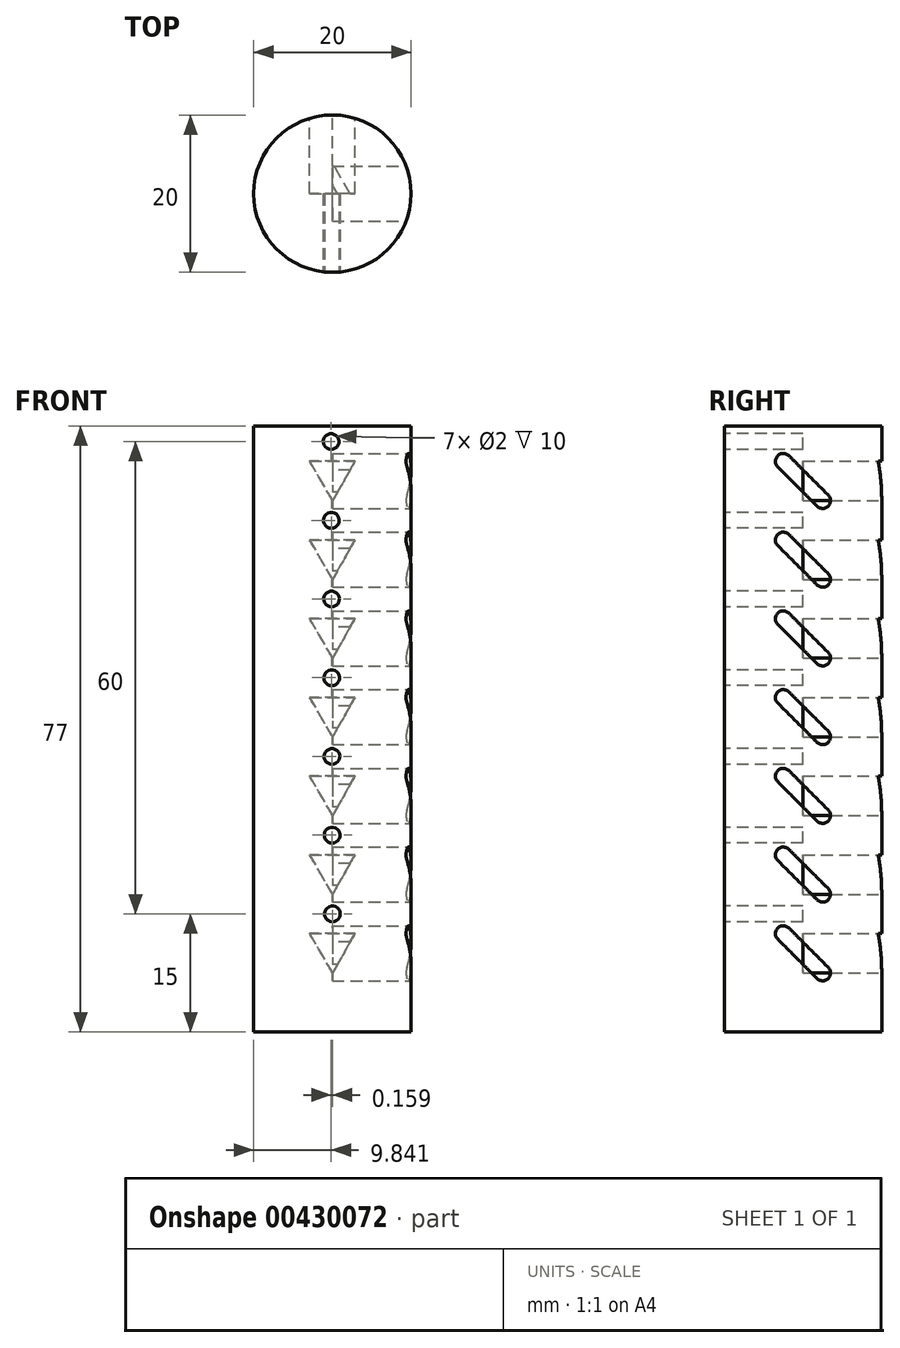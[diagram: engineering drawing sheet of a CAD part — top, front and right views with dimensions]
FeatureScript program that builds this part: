
annotation { "Feature Type Name" : "Feature", "Feature Type Description" : "" }
export const myFeature = defineFeature(function(context is Context, id is Id, definition is map)
    precondition{}
    {
        {
            var Q0;
            Q0=qCreatedBy(makeId("Top.planeOp"),FACE);
            var sketch = newSketch(context, id + "F0", { "sketchPlane" : qUnion([Q0])});
            skCircle(sketch, "E0", {"center": v(0, 0) * mm, "radius": 10 * mm});
            skSolve(sketch);
        }
        {
            var Q0;
            Q0=makeQuery(id+"F0.imprint","IMPRINT",FACE,{"disambiguationData":[TD([[makeQuery(id+"F0.imprint","IMPRINT",EDGE,{"derivedFrom":sQuery(id+"F0.wireOp",EDGE,"E0")}),1.0]])]});
            extrude(context, id + "F1", {"entities" : qUnion([Q0]), "depth" : (7 * 10 + 7) * mm});
        }
        {
            var Q0;
            Q0=qCreatedBy(makeId("Front.planeOp"),FACE);
            cPlane(context, id + "F2", {"entities" : qUnion([Q0]), "cplaneType" : CPlaneType.OFFSET, "offset" : 10 * mm, "width" : 150 * mm, "height" : 150 * mm});
        }
        {
            var Q0;
            Q0=qCreatedBy(id+"F2.planeOp",FACE);
            var sketch = newSketch(context, id + "F3", { "sketchPlane" : qUnion([Q0])});
            skCircle(sketch, "E1", {"center": v(0, 15) * mm, "radius": 1 * mm});
            skCircle(sketch, "E2.1.0.0", {"center": v(-0.03, 25) * mm, "radius": 1 * mm});
            skCircle(sketch, "E2.2.0.0", {"center": v(-0.05, 35) * mm, "radius": 1 * mm});
            skCircle(sketch, "E2.3.0.0", {"center": v(-0.08, 45) * mm, "radius": 1 * mm});
            skCircle(sketch, "E2.4.0.0", {"center": v(-0.1, 55) * mm, "radius": 1 * mm});
            skCircle(sketch, "E2.5.0.0", {"center": v(-0.13, 65) * mm, "radius": 1 * mm});
            skCircle(sketch, "E2.6.0.0", {"center": v(-0.16, 75) * mm, "radius": 1 * mm});
            skLineSegment(sketch, "E2.direction1", {"start": v(0, 15) * mm, "end": v(-0.03, 25) * mm, "construction": true});
            skSolve(sketch);
        }
        {
            var Q0;
            Q0=qSketchRegion(id+"F3",true);
            extrude(context, id + "F4", {"entities" : qUnion([Q0]), "operationType" : NewBodyOperationType.REMOVE, "oppositeDirection" : true, "depth" : 10 * mm});
        }
        {
            var Q0;
            Q0=qCreatedBy(makeId("Right.planeOp"),FACE);
            cPlane(context, id + "F5", {"entities" : qUnion([Q0]), "cplaneType" : CPlaneType.OFFSET, "offset" : 10 * mm, "width" : 150 * mm, "height" : 150 * mm});
        }
        {
            var Q0;
            Q0=qCreatedBy(id+"F5.planeOp",FACE);
            var sketch = newSketch(context, id + "F6", { "sketchPlane" : qUnion([Q0])});
            skLineSegment(sketch, "E3", {"start": v(-2.5, 12.5) * mm, "end": v(2.5, 7.5) * mm, "construction": true});
            skLineSegment(sketch, "E4", {"start": v(2.5, 7.5) * mm, "end": v(0, 7.5) * mm, "construction": true});
            skPoint(sketch, "E4.endSnap0", {"position": v(0, 10) * mm});
            skArc(sketch, "E5.0.startCap", {"start": v(-3.2, 11.8) * mm, "mid": v(-3.2, 13.2) * mm, "end": v(-1.8, 13.2) * mm});
            skArc(sketch, "E5.0.endCap", {"start": v(3.2, 8.2) * mm, "mid": v(3.2, 6.8) * mm, "end": v(1.8, 6.8) * mm});
            skLineSegment(sketch, "E5.0.left", {"start": v(-1.8, 13.2) * mm, "end": v(3.2, 8.2) * mm});
            skLineSegment(sketch, "E5.0.right", {"start": v(-3.2, 11.8) * mm, "end": v(1.8, 6.8) * mm});
            skLineSegment(sketch, "E6.1.0.0", {"start": v(-2.5, 22.5) * mm, "end": v(2.5, 17.5) * mm, "construction": true});
            skArc(sketch, "E6.1.0.1", {"start": v(-3.2, 21.8) * mm, "mid": v(-3.2, 23.2) * mm, "end": v(-1.8, 23.2) * mm});
            skLineSegment(sketch, "E6.1.0.2", {"start": v(-3.2, 21.8) * mm, "end": v(1.8, 16.8) * mm});
            skLineSegment(sketch, "E6.1.0.3", {"start": v(-1.8, 23.2) * mm, "end": v(3.2, 18.2) * mm});
            skLineSegment(sketch, "E6.1.0.4", {"start": v(2.5, 17.5) * mm, "end": v(0, 17.5) * mm, "construction": true});
            skPoint(sketch, "E6.1.0.5", {"position": v(0, 20) * mm});
            skArc(sketch, "E6.1.0.6", {"start": v(3.2, 18.2) * mm, "mid": v(3.2, 16.8) * mm, "end": v(1.8, 16.8) * mm});
            skLineSegment(sketch, "E6.2.0.0", {"start": v(-2.5, 32.5) * mm, "end": v(2.5, 27.5) * mm, "construction": true});
            skArc(sketch, "E6.2.0.1", {"start": v(-3.2, 31.8) * mm, "mid": v(-3.2, 33.2) * mm, "end": v(-1.8, 33.2) * mm});
            skLineSegment(sketch, "E6.2.0.2", {"start": v(-3.2, 31.8) * mm, "end": v(1.8, 26.8) * mm});
            skLineSegment(sketch, "E6.2.0.3", {"start": v(-1.8, 33.2) * mm, "end": v(3.2, 28.2) * mm});
            skLineSegment(sketch, "E6.2.0.4", {"start": v(2.5, 27.5) * mm, "end": v(0, 27.5) * mm, "construction": true});
            skPoint(sketch, "E6.2.0.5", {"position": v(0, 30) * mm});
            skArc(sketch, "E6.2.0.6", {"start": v(3.2, 28.2) * mm, "mid": v(3.2, 26.8) * mm, "end": v(1.8, 26.8) * mm});
            skLineSegment(sketch, "E6.3.0.0", {"start": v(-2.5, 42.5) * mm, "end": v(2.5, 37.5) * mm, "construction": true});
            skArc(sketch, "E6.3.0.1", {"start": v(-3.2, 41.8) * mm, "mid": v(-3.2, 43.2) * mm, "end": v(-1.8, 43.2) * mm});
            skLineSegment(sketch, "E6.3.0.2", {"start": v(-3.2, 41.8) * mm, "end": v(1.8, 36.8) * mm});
            skLineSegment(sketch, "E6.3.0.3", {"start": v(-1.8, 43.2) * mm, "end": v(3.2, 38.2) * mm});
            skLineSegment(sketch, "E6.3.0.4", {"start": v(2.5, 37.5) * mm, "end": v(0, 37.5) * mm, "construction": true});
            skPoint(sketch, "E6.3.0.5", {"position": v(0, 40) * mm});
            skArc(sketch, "E6.3.0.6", {"start": v(3.2, 38.2) * mm, "mid": v(3.2, 36.8) * mm, "end": v(1.8, 36.8) * mm});
            skLineSegment(sketch, "E6.4.0.0", {"start": v(-2.5, 52.5) * mm, "end": v(2.5, 47.5) * mm, "construction": true});
            skArc(sketch, "E6.4.0.1", {"start": v(-3.2, 51.8) * mm, "mid": v(-3.2, 53.2) * mm, "end": v(-1.8, 53.2) * mm});
            skLineSegment(sketch, "E6.4.0.2", {"start": v(-3.2, 51.8) * mm, "end": v(1.8, 46.8) * mm});
            skLineSegment(sketch, "E6.4.0.3", {"start": v(-1.8, 53.2) * mm, "end": v(3.2, 48.2) * mm});
            skLineSegment(sketch, "E6.4.0.4", {"start": v(2.5, 47.5) * mm, "end": v(0, 47.5) * mm, "construction": true});
            skPoint(sketch, "E6.4.0.5", {"position": v(0, 50) * mm});
            skArc(sketch, "E6.4.0.6", {"start": v(3.2, 48.2) * mm, "mid": v(3.2, 46.8) * mm, "end": v(1.8, 46.8) * mm});
            skLineSegment(sketch, "E6.5.0.0", {"start": v(-2.5, 62.5) * mm, "end": v(2.5, 57.5) * mm, "construction": true});
            skArc(sketch, "E6.5.0.1", {"start": v(-3.2, 61.8) * mm, "mid": v(-3.2, 63.2) * mm, "end": v(-1.8, 63.2) * mm});
            skLineSegment(sketch, "E6.5.0.2", {"start": v(-3.2, 61.8) * mm, "end": v(1.8, 56.8) * mm});
            skLineSegment(sketch, "E6.5.0.3", {"start": v(-1.8, 63.2) * mm, "end": v(3.2, 58.2) * mm});
            skLineSegment(sketch, "E6.5.0.4", {"start": v(2.5, 57.5) * mm, "end": v(0, 57.5) * mm, "construction": true});
            skPoint(sketch, "E6.5.0.5", {"position": v(0, 60) * mm});
            skArc(sketch, "E6.5.0.6", {"start": v(3.2, 58.2) * mm, "mid": v(3.2, 56.8) * mm, "end": v(1.8, 56.8) * mm});
            skLineSegment(sketch, "E6.6.0.0", {"start": v(-2.5, 72.5) * mm, "end": v(2.5, 67.5) * mm, "construction": true});
            skArc(sketch, "E6.6.0.1", {"start": v(-3.2, 71.8) * mm, "mid": v(-3.2, 73.2) * mm, "end": v(-1.8, 73.2) * mm});
            skLineSegment(sketch, "E6.6.0.2", {"start": v(-3.2, 71.8) * mm, "end": v(1.8, 66.8) * mm});
            skLineSegment(sketch, "E6.6.0.3", {"start": v(-1.8, 73.2) * mm, "end": v(3.2, 68.2) * mm});
            skLineSegment(sketch, "E6.6.0.4", {"start": v(2.5, 67.5) * mm, "end": v(0, 67.5) * mm, "construction": true});
            skPoint(sketch, "E6.6.0.5", {"position": v(0, 70) * mm});
            skArc(sketch, "E6.6.0.6", {"start": v(3.2, 68.2) * mm, "mid": v(3.2, 66.8) * mm, "end": v(1.8, 66.8) * mm});
            skLineSegment(sketch, "E6.direction1", {"start": v(0, 7.5) * mm, "end": v(0, 17.5) * mm, "construction": true});
            skSolve(sketch);
        }
        {
            var Q0;
            Q0=qSketchRegion(id+"F6",true);
            extrude(context, id + "F7", {"entities" : qUnion([Q0]), "operationType" : NewBodyOperationType.REMOVE, "oppositeDirection" : true, "depth" : 10 * mm});
        }
        {
            var Q0;
            Q0=qCreatedBy(makeId("Front.planeOp"),FACE);
            cPlane(context, id + "F8", {"entities" : qUnion([Q0]), "cplaneType" : CPlaneType.OFFSET, "offset" : 10 * mm, "oppositeDirection" : true, "width" : 150 * mm, "height" : 150 * mm});
        }
        {
            var Q0;
            Q0=qCreatedBy(id+"F8.planeOp",FACE);
            var sketch = newSketch(context, id + "F9", { "sketchPlane" : qUnion([Q0])});
            skLineSegment(sketch, "E7", {"start": v(-2.89, 12.5) * mm, "end": v(0, 7.5) * mm});
            skLineSegment(sketch, "E8", {"start": v(0, 7.5) * mm, "end": v(2.89, 12.5) * mm});
            skLineSegment(sketch, "E9", {"start": v(2.89, 12.5) * mm, "end": v(-2.89, 12.5) * mm});
            skLineSegment(sketch, "E10.1.0.0", {"start": v(0, 17.5) * mm, "end": v(2.89, 22.5) * mm});
            skLineSegment(sketch, "E10.1.0.1", {"start": v(2.89, 22.5) * mm, "end": v(-2.89, 22.5) * mm});
            skLineSegment(sketch, "E10.1.0.2", {"start": v(-2.89, 22.5) * mm, "end": v(0, 17.5) * mm});
            skLineSegment(sketch, "E10.2.0.0", {"start": v(0, 27.5) * mm, "end": v(2.89, 32.5) * mm});
            skLineSegment(sketch, "E10.2.0.1", {"start": v(2.89, 32.5) * mm, "end": v(-2.89, 32.5) * mm});
            skLineSegment(sketch, "E10.2.0.2", {"start": v(-2.89, 32.5) * mm, "end": v(0, 27.5) * mm});
            skLineSegment(sketch, "E10.3.0.0", {"start": v(0, 37.5) * mm, "end": v(2.89, 42.5) * mm});
            skLineSegment(sketch, "E10.3.0.1", {"start": v(2.89, 42.5) * mm, "end": v(-2.89, 42.5) * mm});
            skLineSegment(sketch, "E10.3.0.2", {"start": v(-2.89, 42.5) * mm, "end": v(0, 37.5) * mm});
            skLineSegment(sketch, "E10.4.0.0", {"start": v(0, 47.5) * mm, "end": v(2.89, 52.5) * mm});
            skLineSegment(sketch, "E10.4.0.1", {"start": v(2.89, 52.5) * mm, "end": v(-2.89, 52.5) * mm});
            skLineSegment(sketch, "E10.4.0.2", {"start": v(-2.89, 52.5) * mm, "end": v(0, 47.5) * mm});
            skLineSegment(sketch, "E10.5.0.0", {"start": v(0, 57.5) * mm, "end": v(2.89, 62.5) * mm});
            skLineSegment(sketch, "E10.5.0.1", {"start": v(2.89, 62.5) * mm, "end": v(-2.89, 62.5) * mm});
            skLineSegment(sketch, "E10.5.0.2", {"start": v(-2.89, 62.5) * mm, "end": v(0, 57.5) * mm});
            skLineSegment(sketch, "E10.6.0.0", {"start": v(0, 67.5) * mm, "end": v(2.89, 72.5) * mm});
            skLineSegment(sketch, "E10.6.0.1", {"start": v(2.89, 72.5) * mm, "end": v(-2.89, 72.5) * mm});
            skLineSegment(sketch, "E10.6.0.2", {"start": v(-2.89, 72.5) * mm, "end": v(0, 67.5) * mm});
            skLineSegment(sketch, "E10.direction1", {"start": v(0, 7.5) * mm, "end": v(0, 17.5) * mm, "construction": true});
            skSolve(sketch);
        }
        {
            var Q0;
            Q0=qSketchRegion(id+"F9",true);
            extrude(context, id + "F10", {"entities" : qUnion([Q0]), "operationType" : NewBodyOperationType.REMOVE, "depth" : 10 * mm});
        }
    });
